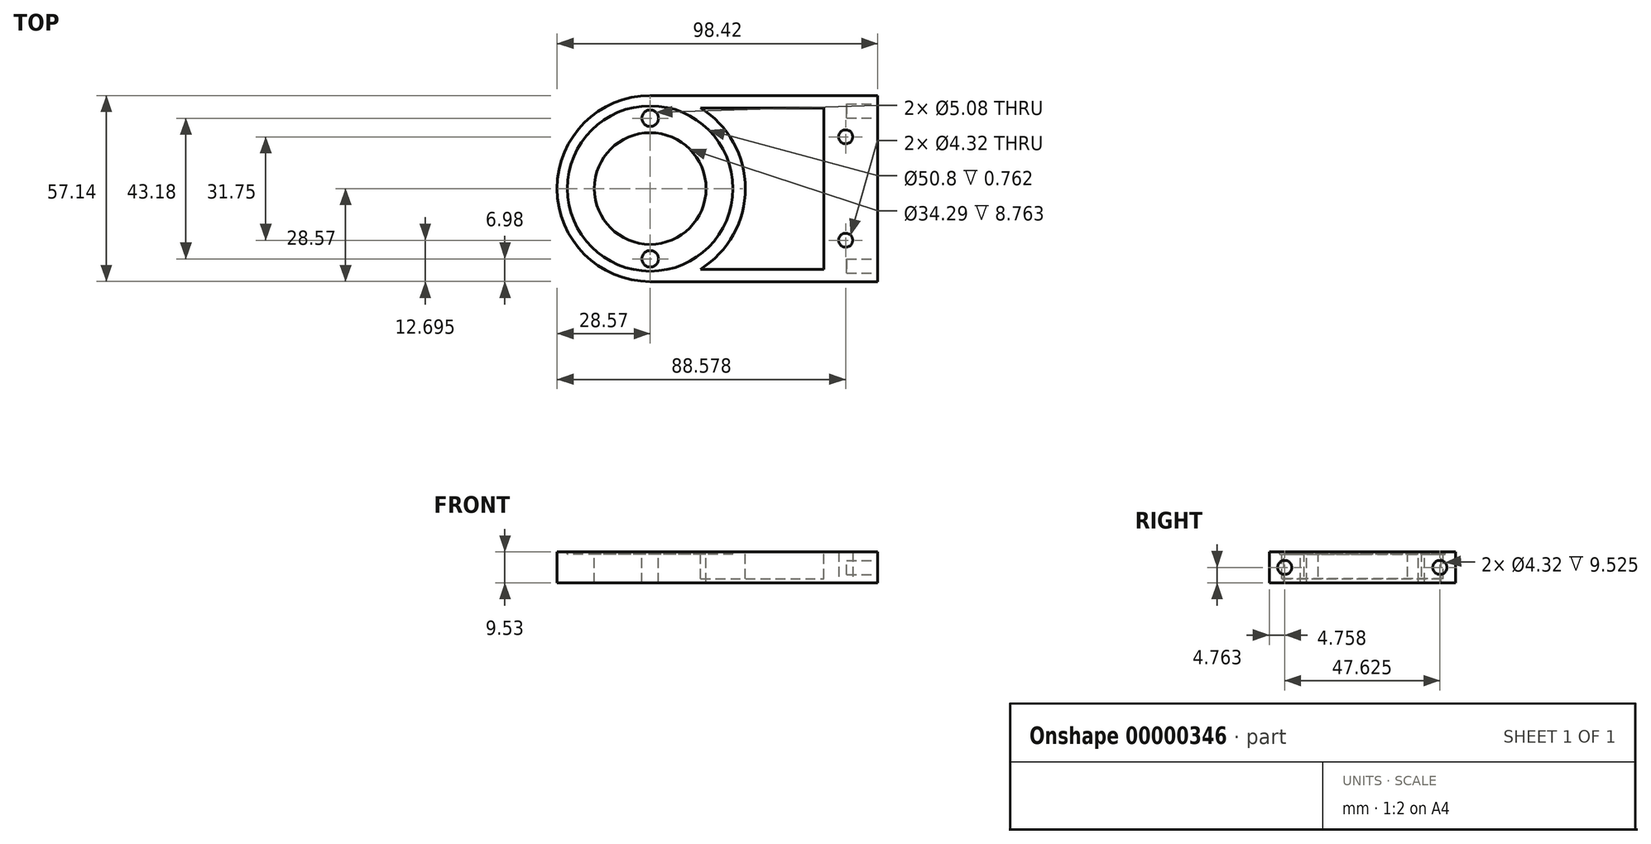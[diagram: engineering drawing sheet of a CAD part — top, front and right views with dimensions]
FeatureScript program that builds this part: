
annotation { "Feature Type Name" : "Feature", "Feature Type Description" : "" }
export const myFeature = defineFeature(function(context is Context, id is Id, definition is map)
    precondition{}
    {
        {
            var Q0;
            Q0=qCreatedBy(makeId("Top.planeOp"),FACE);
            var sketch = newSketch(context, id + "F0", { "sketchPlane" : qUnion([Q0])});
            skCircle(sketch, "E0", {"center": v(0, 0) * mm, "radius": 28.58 * mm});
            skLineSegment(sketch, "E1.bottom", {"start": v(0, 28.58) * mm, "end": v(69.85, 28.58) * mm});
            skLineSegment(sketch, "E1.top", {"start": v(0, -28.58) * mm, "end": v(69.85, -28.58) * mm});
            skLineSegment(sketch, "E1.left", {"start": v(0, 28.58) * mm, "end": v(0, -28.58) * mm});
            skLineSegment(sketch, "E1.right", {"start": v(69.85, 28.58) * mm, "end": v(69.85, -28.58) * mm});
            skSolve(sketch);
        }
        {
            var Q0;
            {var subQ0=sQuery(id+"F0.wireOp",EDGE,"E1.left");var subQ1=makeQuery(id+"F0.imprint","IMPRINT",EDGE,{"derivedFrom":subQ0});var subQ5=sQuery(id+"F0.wireOp",EDGE,"E1.bottom");Q0=qUnion([makeQuery(id+"F0.imprint","IMPRINT",FACE,{"disambiguationData":[TD([[subQ1,-1.0]])]}),makeQuery(id+"F0.imprint","IMPRINT",FACE,{"disambiguationData":[TD([[makeQuery(id+"F0.imprint","IMPRINT",EDGE,{"derivedFrom":subQ5}),-1.0]])]}),makeQuery(id+"F0.imprint","IMPRINT",FACE,{"disambiguationData":[TD([[subQ1,1.0]])]})]);}
            extrude(context, id + "F1", {"entities" : qUnion([Q0]), "depth" : 9.52 * mm});
        }
        {
            var Q0;
            Q0=makeQuery(id+"F1.opExtrude","CAP_FACE",FACE,{"disambiguationData":[OSD([sQuery(id+"F0.wireOp",EDGE,"E0"),sQuery(id+"F0.wireOp",EDGE,"E1.bottom"),sQuery(id+"F0.wireOp",EDGE,"E1.top"),sQuery(id+"F0.wireOp",EDGE,"E1.right")])],"isStart":false});
            var sketch = newSketch(context, id + "F2", { "sketchPlane" : qUnion([Q0])});
            skCircle(sketch, "E2", {"center": v(0, 0) * mm, "radius": 25.4 * mm});
            skPoint(sketch, "E3.visualSharp", {"position": v(63.5, 25.4) * mm});
            skPoint(sketch, "E4.visualSharp", {"position": v(63.5, -25.4) * mm});
            skSolve(sketch);
        }
        {
            var Q0;
            Q0=makeQuery(id+"F2.imprint","IMPRINT",FACE,{"disambiguationData":[TD([[makeQuery(id+"F2.imprint","IMPRINT",EDGE,{"derivedFrom":sQuery(id+"F2.wireOp",EDGE,"E2")}),1.0]])]});
            extrude(context, id + "F3", {"entities" : qUnion([Q0]), "operationType" : NewBodyOperationType.REMOVE, "oppositeDirection" : true, "depth" : 0.76 * mm});
        }
        {
            var Q0;
            Q0=makeQuery(id+"F3.boolean.opBoolean","COPY",FACE,{"derivedFrom":makeQuery(id+"F3.opExtrude","CAP_FACE",FACE,{"disambiguationData":[OSD([sQuery(id+"F2.wireOp",EDGE,"E2")])],"isStart":false})});
            var sketch = newSketch(context, id + "F4", { "sketchPlane" : qUnion([Q0])});
            skCircle(sketch, "E5", {"center": v(0, 0) * mm, "radius": 17.15 * mm});
            skCircle(sketch, "E6", {"center": v(0, 0) * mm, "radius": 21.59 * mm, "construction": true});
            skCircle(sketch, "E7", {"center": v(0, 21.59) * mm, "radius": 2.54 * mm});
            skCircle(sketch, "E8", {"center": v(0, -21.59) * mm, "radius": 2.54 * mm});
            skSolve(sketch);
        }
        {
            var Q0;
            {Q0=qUnion([makeQuery(id+"F4.imprint","IMPRINT",FACE,{"disambiguationData":[TD([[makeQuery(id+"F4.imprint","IMPRINT",EDGE,{"derivedFrom":sQuery(id+"F4.wireOp",EDGE,"E5")}),1.0]])]}),makeQuery(id+"F4.imprint","IMPRINT",FACE,{"disambiguationData":[TD([[makeQuery(id+"F4.imprint","IMPRINT",EDGE,{"derivedFrom":sQuery(id+"F4.wireOp",EDGE,"E7")}),1.0]])]}),makeQuery(id+"F4.imprint","IMPRINT",FACE,{"disambiguationData":[TD([[makeQuery(id+"F4.imprint","IMPRINT",EDGE,{"derivedFrom":sQuery(id+"F4.wireOp",EDGE,"E8")}),1.0]])]})]);}
            extrude(context, id + "F5", {"entities" : qUnion([Q0]), "operationType" : NewBodyOperationType.REMOVE, "endBound" : BoundingType.THROUGH_ALL, "oppositeDirection" : true, "depth" : 25.4 * mm});
        }
        {
            var Q0;
            Q0=makeQuery(id+"F1.opExtrude","CAP_FACE",FACE,{"disambiguationData":[OSD([sQuery(id+"F0.wireOp",EDGE,"E0"),sQuery(id+"F0.wireOp",EDGE,"E1.bottom"),sQuery(id+"F0.wireOp",EDGE,"E1.top"),sQuery(id+"F0.wireOp",EDGE,"E1.right")])],"isStart":true});
            var sketch = newSketch(context, id + "F6", { "sketchPlane" : qUnion([Q0])});
            skCircle(sketch, "E9", {"center": v(60, 15.88) * mm, "radius": 2.16 * mm});
            skCircle(sketch, "E10", {"center": v(60, -15.88) * mm, "radius": 2.16 * mm});
            skSolve(sketch);
        }
        {
            var Q0;
            {Q0=qUnion([makeQuery(id+"F6.imprint","IMPRINT",FACE,{"disambiguationData":[TD([[makeQuery(id+"F6.imprint","IMPRINT",EDGE,{"derivedFrom":sQuery(id+"F6.wireOp",EDGE,"E9")}),1.0]])]}),makeQuery(id+"F6.imprint","IMPRINT",FACE,{"disambiguationData":[TD([[makeQuery(id+"F6.imprint","IMPRINT",EDGE,{"derivedFrom":sQuery(id+"F6.wireOp",EDGE,"E10")}),1.0]])]})]);}
            extrude(context, id + "F7", {"entities" : qUnion([Q0]), "operationType" : NewBodyOperationType.REMOVE, "endBound" : BoundingType.THROUGH_ALL, "oppositeDirection" : true, "depth" : 25.4 * mm});
        }
        {
            var Q0;
            Q0=makeQuery(id+"F1.opExtrude","SWEPT_FACE",FACE,{"disambiguationData":[OSD([sQuery(id+"F0.wireOp",EDGE,"E1.right")])]});
            var sketch = newSketch(context, id + "F8", { "sketchPlane" : qUnion([Q0])});
            skCircle(sketch, "E11", {"center": v(-23.81, 4.76) * mm, "radius": 2.16 * mm});
            skCircle(sketch, "E12", {"center": v(23.81, 4.76) * mm, "radius": 2.16 * mm});
            skSolve(sketch);
        }
        {
            var Q0;
            {Q0=qUnion([makeQuery(id+"F8.imprint","IMPRINT",FACE,{"disambiguationData":[TD([[makeQuery(id+"F8.imprint","IMPRINT",EDGE,{"derivedFrom":sQuery(id+"F8.wireOp",EDGE,"E11")}),1.0]])]}),makeQuery(id+"F8.imprint","IMPRINT",FACE,{"disambiguationData":[TD([[makeQuery(id+"F8.imprint","IMPRINT",EDGE,{"derivedFrom":sQuery(id+"F8.wireOp",EDGE,"E12")}),1.0]])]})]);}
            extrude(context, id + "F9", {"entities" : qUnion([Q0]), "operationType" : NewBodyOperationType.REMOVE, "oppositeDirection" : true, "depth" : 9.52 * mm});
        }
        {
            var Q0;
            Q0=makeQuery(id+"F1.opExtrude","CAP_FACE",FACE,{"disambiguationData":[OSD([sQuery(id+"F0.wireOp",EDGE,"E0"),sQuery(id+"F0.wireOp",EDGE,"E1.bottom"),sQuery(id+"F0.wireOp",EDGE,"E1.top"),sQuery(id+"F0.wireOp",EDGE,"E1.right")])],"isStart":false});
            var sketch = newSketch(context, id + "F10", { "sketchPlane" : qUnion([Q0])});
            skArc(sketch, "E13.0", {"start": v(15.49, -24.77) * mm, "mid": v(29.21, 0) * mm, "end": v(15.49, 24.77) * mm});
            skLineSegment(sketch, "E14.0", {"start": v(15.49, 24.77) * mm, "end": v(53.34, 24.77) * mm});
            skLineSegment(sketch, "E15.0", {"start": v(15.49, -24.77) * mm, "end": v(53.34, -24.77) * mm});
            skLineSegment(sketch, "E16.0", {"start": v(53.34, 24.77) * mm, "end": v(53.34, -24.77) * mm});
            skSolve(sketch);
        }
        {
            var Q0;
            Q0 = qSketchRegion(id + "F10", true);
            extrude(context, id + "F11", {"entities" : qUnion([Q0]), "operationType" : NewBodyOperationType.REMOVE, "oppositeDirection" : true, "depth" : 8.25 * mm});
        }
    });
